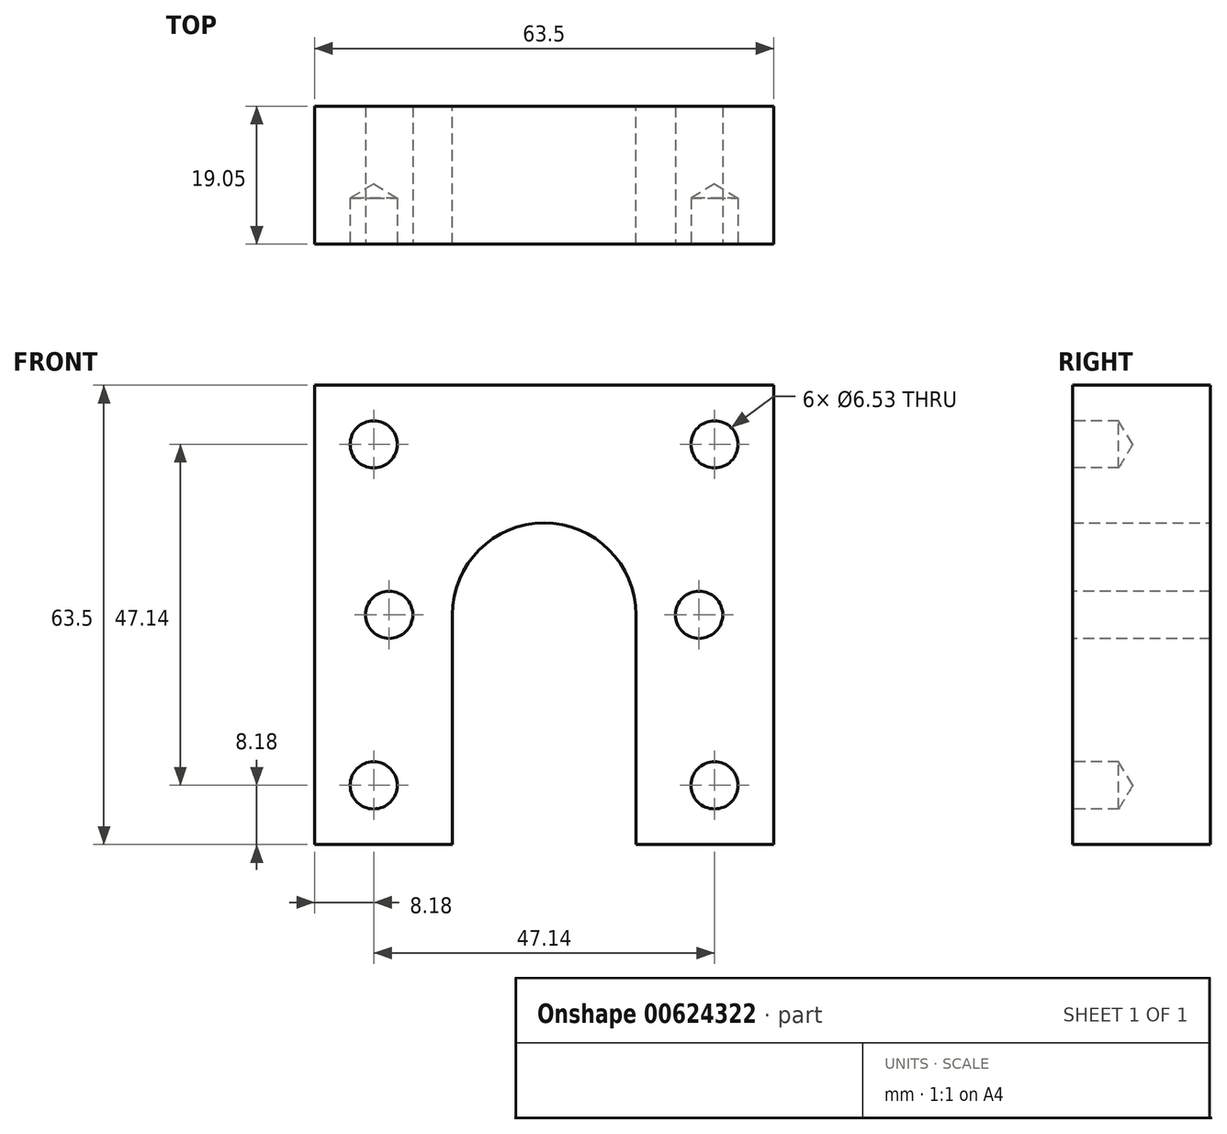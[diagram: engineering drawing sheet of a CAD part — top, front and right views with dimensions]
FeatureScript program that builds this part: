
annotation { "Feature Type Name" : "Feature", "Feature Type Description" : "" }
export const myFeature = defineFeature(function(context is Context, id is Id, definition is map)
    precondition{}
    {
        {
            var Q0;
            Q0=qCreatedBy(makeId("Front.planeOp"),FACE);
            var sketch = newSketch(context, id + "F0", { "sketchPlane" : qUnion([Q0])});
            skLineSegment(sketch, "E0.bottom", {"start": v(-31.75, 31.75) * mm, "end": v(31.75, 31.75) * mm});
            skLineSegment(sketch, "E0.top", {"start": v(-31.75, -31.75) * mm, "end": v(-12.7, -31.75) * mm});
            skLineSegment(sketch, "E0.left", {"start": v(-31.75, 31.75) * mm, "end": v(-31.75, -31.75) * mm});
            skLineSegment(sketch, "E0.right", {"start": v(31.75, 31.75) * mm, "end": v(31.75, -31.75) * mm});
            skLineSegment(sketch, "E1", {"start": v(0, 31.75) * mm, "end": v(0, -31.75) * mm, "construction": true});
            skLineSegment(sketch, "E2", {"start": v(-31.75, 0) * mm, "end": v(31.75, 0) * mm, "construction": true});
            skArc(sketch, "E3", {"start": v(12.7, 0) * mm, "mid": v(0, 12.7) * mm, "end": v(-12.7, 0) * mm});
            skLineSegment(sketch, "E4", {"start": v(-12.7, 0) * mm, "end": v(-12.7, -31.75) * mm});
            skLineSegment(sketch, "E5", {"start": v(12.7, 0) * mm, "end": v(12.7, -31.75) * mm});
            skLineSegment(sketch, "E6.trimOffspring", {"start": v(12.7, -31.75) * mm, "end": v(31.75, -31.75) * mm});
            skSolve(sketch);
        }
        {
            var Q0;
            Q0=makeQuery(id+"F0.imprint","IMPRINT",FACE,{"disambiguationData":[TD([[makeQuery(id+"F0.imprint","IMPRINT",EDGE,{"derivedFrom":sQuery(id+"F0.wireOp",EDGE,"E0.bottom")}),-1.0]])]});
            extrude(context, id + "F1", {"entities" : qUnion([Q0]), "depth" : 19.05 * mm, "offsetDistance" : 25.4 * mm});
        }
        {
            var Q0;
            Q0=makeQuery(id+"F1.opExtrude","CAP_FACE",FACE,{"disambiguationData":[OSD([sQuery(id+"F0.wireOp",EDGE,"E0.bottom"),sQuery(id+"F0.wireOp",EDGE,"E0.top"),sQuery(id+"F0.wireOp",EDGE,"E0.left"),sQuery(id+"F0.wireOp",EDGE,"E0.right"),sQuery(id+"F0.wireOp",EDGE,"E3")])],"isStart":false});
            var sketch = newSketch(context, id + "F2", { "sketchPlane" : qUnion([Q0])});
            skPoint(sketch, "E7", {"position": v(-23.57, 23.57) * mm});
            skPoint(sketch, "E8", {"position": v(23.57, 23.57) * mm});
            skPoint(sketch, "E9", {"position": v(-23.57, -23.57) * mm});
            skPoint(sketch, "E10", {"position": v(23.57, -23.57) * mm});
            skSolve(sketch);
        }
        {
            var Q0;
            Q0=sQuery(id+"F2.wireOp",VERTEX,"E7");
            var Q1;
            Q1=sQuery(id+"F2.wireOp",VERTEX,"E9");
            var Q2;
            Q2=sQuery(id+"F2.wireOp",VERTEX,"E10");
            var Q3;
            Q3=sQuery(id+"F2.wireOp",VERTEX,"E8");
            var Q4;
            Q4=makeQuery(id+"F1.opExtrude","SWEPT_BODY",BODY,{"disambiguationData":[OSD([sQuery(id+"F0.wireOp",EDGE,"E0.bottom"),sQuery(id+"F0.wireOp",EDGE,"E0.top"),sQuery(id+"F0.wireOp",EDGE,"E0.left"),sQuery(id+"F0.wireOp",EDGE,"E0.right"),sQuery(id+"F0.wireOp",EDGE,"E3")])]});
            hole(context, id + "F3", {"style" : HoleStyle.SIMPLE, "endStyle" : HoleEndStyle.BLIND, "standardTappedOrClearance" : lookupTablePath({ "standard" : "ANSI", "fit" : "Close", "size" : "1/4", "type" : "Clearance" }), "standardBlindInLast" : lookupTablePath({ "fit" : "Close", "standard" : "ANSI", "size" : "1/4", "type" : "Clearance" }), "holeDiameter" : 6.53 * mm, "majorDiameter" : 6.35 * mm, "holeDepth" : 6.35 * mm, "isTappedThrough" : true, "tappedDepth" : 12.7 * mm, "tapClearance" : 3, "startFromSketch" : true, "locations" : qUnion([Q0, Q1, Q2, Q3]), "scope" : qUnion([Q4])});
        }
        {
            var Q0;
            Q0=makeQuery(id+"F1.opExtrude","CAP_FACE",FACE,{"disambiguationData":[OSD([sQuery(id+"F0.wireOp",EDGE,"E0.bottom"),sQuery(id+"F0.wireOp",EDGE,"E0.top"),sQuery(id+"F0.wireOp",EDGE,"E0.left"),sQuery(id+"F0.wireOp",EDGE,"E0.right"),sQuery(id+"F0.wireOp",EDGE,"E3")])],"isStart":false});
            var sketch = newSketch(context, id + "F4", { "sketchPlane" : qUnion([Q0])});
            skPoint(sketch, "E11", {"position": v(-21.43, 0) * mm});
            skPoint(sketch, "E12", {"position": v(21.43, 0) * mm});
            skSolve(sketch);
        }
        {
            var Q0;
            Q0=sQuery(id+"F4.wireOp",VERTEX,"E11");
            var Q1;
            Q1=sQuery(id+"F4.wireOp",VERTEX,"E12");
            var Q2;
            Q2=makeQuery(id+"F1.opExtrude","SWEPT_BODY",BODY,{"disambiguationData":[OSD([sQuery(id+"F0.wireOp",EDGE,"E0.bottom"),sQuery(id+"F0.wireOp",EDGE,"E0.top"),sQuery(id+"F0.wireOp",EDGE,"E0.left"),sQuery(id+"F0.wireOp",EDGE,"E0.right"),sQuery(id+"F0.wireOp",EDGE,"E3")])]});
            hole(context, id + "F5", {"style" : HoleStyle.SIMPLE, "endStyle" : HoleEndStyle.THROUGH, "standardTappedOrClearance" : lookupTablePath({ "standard" : "ANSI", "fit" : "Close", "size" : "1/4", "type" : "Clearance" }), "standardBlindInLast" : lookupTablePath({ "fit" : "Close", "standard" : "ANSI", "size" : "1/4", "type" : "Clearance" }), "holeDiameter" : 6.53 * mm, "majorDiameter" : 6.35 * mm, "isTappedThrough" : true, "tappedDepth" : 12.7 * mm, "tapClearance" : 3, "startFromSketch" : true, "locations" : qUnion([Q0, Q1]), "scope" : qUnion([Q2])});
        }
    });
